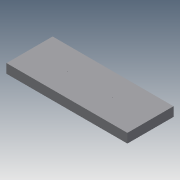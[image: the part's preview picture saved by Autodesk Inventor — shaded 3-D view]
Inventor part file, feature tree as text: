
AUTODESK INVENTOR PART (.ipt)
format: ipt  version: 2013 (Build 170138000, 138)  size: 71,680 bytes
history: native  units: mm
features: extrude x1, sketch x1
ambient origin geometry x8: Origin, YZ Plane, XZ Plane, XY Plane, X Axis, Y Axis, Z Axis, Center Point
bodies: Solid1 (feature_tree)
feature tree (2):
  extrude  "Extrusion1"  Depth=50.0mm
  sketch  "Sketch1"  dims[d0=131.0mm d1=50.0mm d4=0.5mm d5=0.5mm d6=10.0mm d7=0.0mm]
